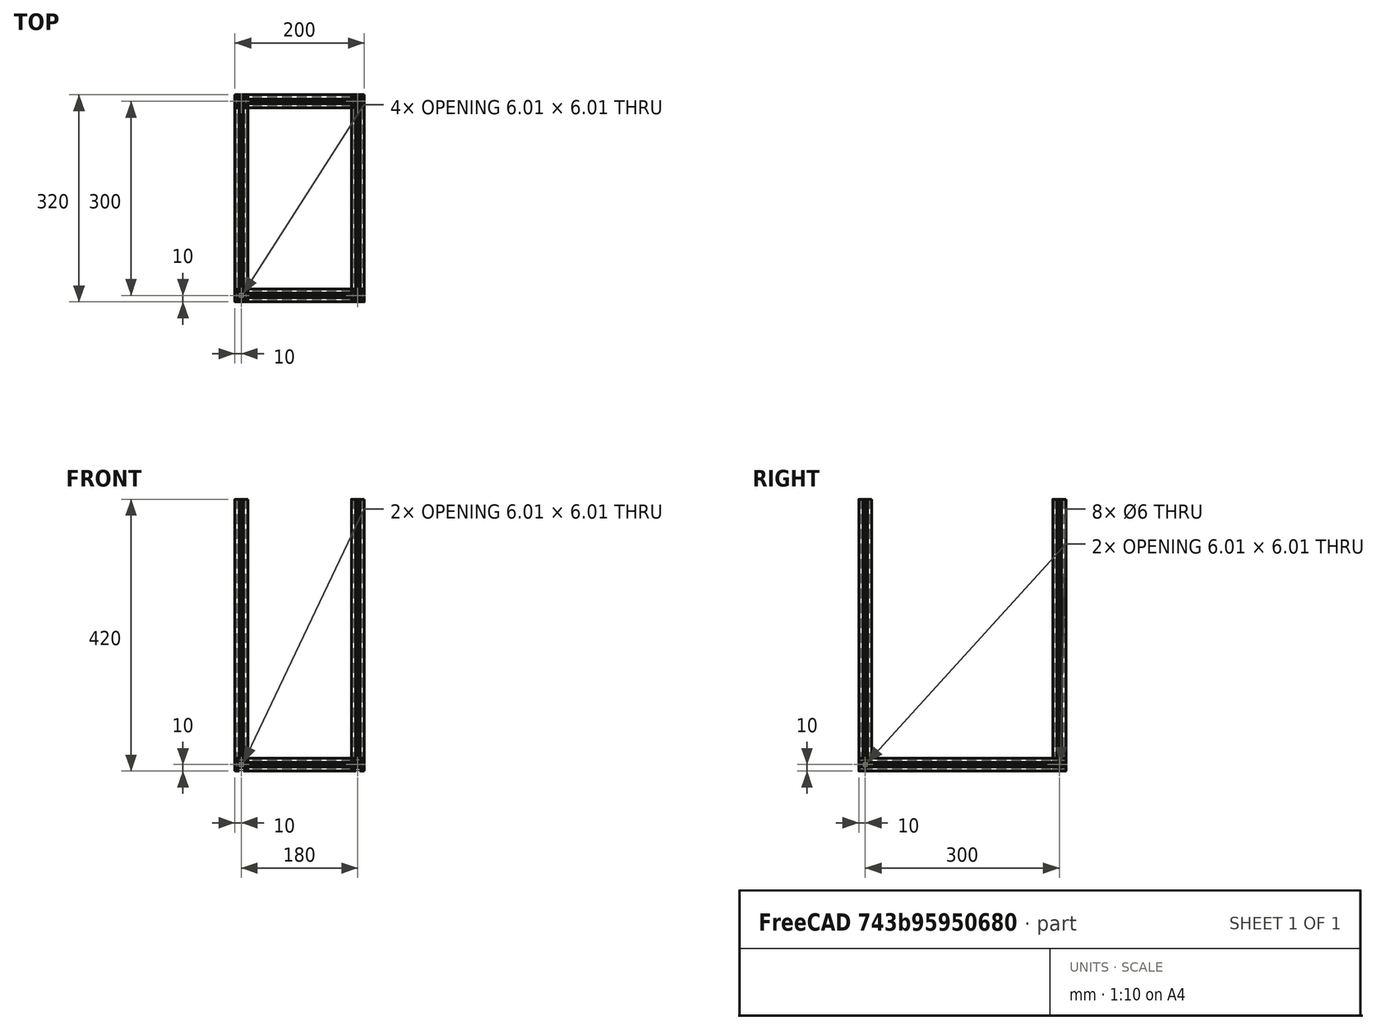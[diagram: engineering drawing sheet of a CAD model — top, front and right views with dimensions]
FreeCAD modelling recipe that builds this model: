
FCSTD DOCUMENT  (FreeCAD 0.17R9796 (Git))
Label: UPKframe3
License: All rights reserved
LicenseURL: http://en.wikipedia.org/wiki/All_rights_reserved
objects: Part::Feature×12, Part::FeaturePython×8, App::Part×2
note: 20 computed .brp shape members not serialized (recipe doc carries the construction recipe); baked Part::Feature solids carry a one-line shape summary decoded from their .brp

FEATURE [Part::Feature] Pocket001001  label="tslot40"
  Placement = pos=(0,0,20) rot=(0,0,1;0rad)
  shape: bbox 20 x 20 x 400 mm, 94 faces (baked)
FEATURE [Part::Feature] Pocket003001  label="tslot32con"
  Placement = pos=(0,10,10) rot=(1,0,0;1.5708rad)
  shape: bbox 20 x 320 x 20 mm, 150 faces (baked)
FEATURE [Part::Feature] Pocket003002  label="tslot16"
  Placement = pos=(10,0,10) rot=(0,1,0;1.5708rad)
  shape: bbox 160 x 20 x 20 mm, 94 faces (baked)
FEATURE [Part::Feature] Pocket003006  label="tslot16_001"
  Placement = pos=(10,-300,10) rot=(0,1,0;1.5708rad)
  shape: bbox 160 x 20 x 20 mm, 94 faces (baked)
FEATURE [Part::Feature] Pocket003007  label="tslot32con_001"
  Placement = pos=(180,-310,10) rot=(0,0.707107,0.707107;3.14159rad)
  shape: bbox 20 x 320 x 20 mm, 150 faces (baked)
FEATURE [Part::FeaturePython] Screw  label="M6x25-Screw"  # Fasteners workbench fastener (typed FeaturePython)
  Placement = pos=(-4,0,10) rot=(0,1,0;4.71239rad)
  diameter = 7
  invert = false
  length = 6
  matchOuter = false
  offset = 0
  thread = false
  type = 15
FEATURE [Part::FeaturePython] Screw001  label="M6x25-Screw004"  # Fasteners workbench fastener (typed FeaturePython)
  Placement = pos=(-4,-300,10) rot=(0,-1,0;1.5708rad)
  diameter = 7
  invert = false
  length = 6
  matchOuter = false
  offset = 0
  thread = false
  type = 15
FEATURE [Part::FeaturePython] Screw002  label="M6x25-Screw005"  # Fasteners workbench fastener (typed FeaturePython)
  Placement = pos=(184,0,10) rot=(0,1,0;1.5708rad)
  diameter = 7
  invert = false
  length = 6
  matchOuter = false
  offset = 0
  thread = false
  type = 15
FEATURE [Part::FeaturePython] Screw004  label="M6x25-Screw006"  # Fasteners workbench fastener (typed FeaturePython)
  Placement = pos=(184,-300,10) rot=(0,1,0;1.5708rad)
  diameter = 7
  invert = false
  length = 6
  matchOuter = false
  offset = 0
  thread = false
  type = 15
FEATURE [App::Part] Part  label="lower_frame"
  Group = -> [Pocket003001,Pocket003002,Pocket003006,Pocket003007,Screw,Screw001,Screw002,Screw004]
  License = CC BY 3.0
  LicenseURL = http://creativecommons.org/licenses/by/3.0/
  Origin = -> PartOrigin
FEATURE [Part::Feature] Pocket003008  label="tslot32con001"
  Placement = pos=(0,10,10) rot=(1,0,0;1.5708rad)
  shape: bbox 20 x 320 x 20 mm, 150 faces (baked)
FEATURE [Part::Feature] Pocket003009  label="tslot041"
  Placement = pos=(10,0,10) rot=(0,1,0;1.5708rad)
  shape: bbox 160 x 20 x 20 mm, 94 faces (baked)
FEATURE [Part::Feature] Pocket003010  label="tslot16_002"
  Placement = pos=(10,-300,10) rot=(0,1,0;1.5708rad)
  shape: bbox 160 x 20 x 20 mm, 94 faces (baked)
FEATURE [Part::Feature] Pocket003011  label="tslot32con_002"
  Placement = pos=(180,-310,10) rot=(0,0.707107,0.707107;3.14159rad)
  shape: bbox 20 x 320 x 20 mm, 150 faces (baked)
FEATURE [Part::FeaturePython] Screw005  label="M6x25-Screw007"  # Fasteners workbench fastener (typed FeaturePython)
  Placement = pos=(-4,0,10) rot=(0,-1,0;1.5708rad)
  diameter = 7
  invert = false
  length = 6
  matchOuter = false
  offset = 0
  thread = false
  type = 15
FEATURE [Part::FeaturePython] Screw006  label="M6x25-Screw008"  # Fasteners workbench fastener (typed FeaturePython)
  Placement = pos=(-4,-300,10) rot=(0,-1,0;1.5708rad)
  diameter = 7
  invert = false
  length = 6
  matchOuter = false
  offset = 0
  thread = false
  type = 15
FEATURE [Part::FeaturePython] Screw007  label="M6x25-Screw009"  # Fasteners workbench fastener (typed FeaturePython)
  Placement = pos=(184,0,10) rot=(0,1,0;1.5708rad)
  diameter = 7
  invert = false
  length = 6
  matchOuter = false
  offset = 0
  thread = false
  type = 15
FEATURE [Part::FeaturePython] Screw008  label="M6x25-Screw010"  # Fasteners workbench fastener (typed FeaturePython)
  Placement = pos=(184,-300,10) rot=(0,1,0;1.5708rad)
  diameter = 7
  invert = false
  length = 6
  matchOuter = false
  offset = 0
  thread = false
  type = 15
FEATURE [App::Part] Part001  label="upper_frame"
  Group = -> [Pocket003008,Pocket003009,Pocket003010,Pocket003011,Screw005,Screw006,Screw007,Screw008]
  License = CC BY 3.0
  LicenseURL = http://creativecommons.org/licenses/by/3.0/
  Origin = -> PartOrigin001
  Placement = pos=(0,0,420) rot=(0,0,1;0rad)
FEATURE [Part::Feature] Pocket003012  label="tslot042"
  Placement = pos=(180,0,20) rot=(0,0,1;0rad)
  shape: bbox 20 x 20 x 400 mm, 94 faces (baked)
FEATURE [Part::Feature] Pocket003013  label="tslot043"
  Placement = pos=(180,-300,20) rot=(0,0,1;0rad)
  shape: bbox 20 x 20 x 400 mm, 94 faces (baked)
FEATURE [Part::Feature] Pocket003014  label="tslot044"
  Placement = pos=(0,-300,20) rot=(0,0,1;0rad)
  shape: bbox 20 x 20 x 400 mm, 94 faces (baked)
